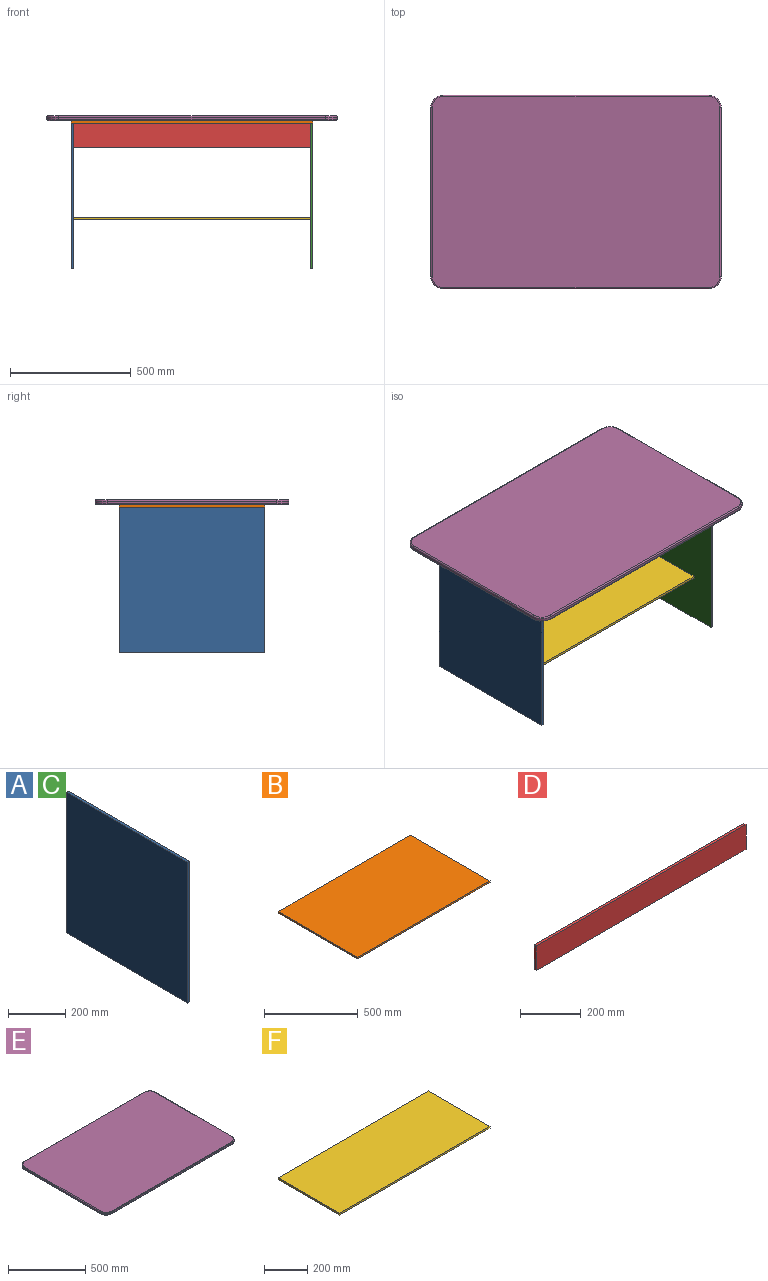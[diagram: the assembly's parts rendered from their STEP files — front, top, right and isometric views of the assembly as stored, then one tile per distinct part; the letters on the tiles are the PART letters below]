
ASSEMBLY  parts=6 mates=5
PART A: 6 faces, bbox 10x600x600 mm
  f0: plane 600x10mm, normal (0,1,0), area 6000mm2, adj f1,f3,f4,f5
  f1: plane 600x10mm, normal (0,0,1), area 6000mm2, adj f0,f2,f4,f5
  f2: plane 600x10mm, normal (0,-1,0), area 6000mm2, adj f1,f3,f4,f5
  f3: plane 600x10mm, normal (0,0,-1), area 6000mm2, adj f0,f2,f4,f5
  f4: plane 600x600mm, normal (1,0,0), area 360000mm2, adj f0,f1,f2,f3
  f5: plane 600x600mm, normal (-1,0,0), area 360000mm2, adj f0,f1,f2,f3
PART B: 6 faces, bbox 1000x600x10 mm
  f0: plane 600x10mm, normal (1,0,0), area 6000mm2, adj f1,f3,f4,f5
  f1: plane 1000x10mm, normal (0,1,0), area 10000mm2, adj f0,f2,f4,f5
  f2: plane 600x10mm, normal (-1,0,0), area 6000mm2, adj f1,f3,f4,f5
  f3: plane 1000x10mm, normal (0,-1,0), area 10000mm2, adj f0,f2,f4,f5
  f4: plane 1000x600mm, normal (0,0,1), area 600000mm2, adj f0,f1,f2,f3
  f5: plane 1000x600mm, normal (0,0,-1), area 600000mm2, adj f0,f1,f2,f3
PART C: same geometry as A
PART D: 6 faces, bbox 980x10x100 mm
  f0: plane 100x10mm, normal (1,0,0), area 1000mm2, adj f1,f3,f4,f5
  f1: plane 980x10mm, normal (0,0,1), area 9800mm2, adj f0,f2,f4,f5
  f2: plane 100x10mm, normal (-1,0,0), area 1000mm2, adj f1,f3,f4,f5
  f3: plane 980x10mm, normal (0,0,-1), area 9800mm2, adj f0,f2,f4,f5
  f4: plane 980x100mm, normal (0,-1,0), area 98000mm2, adj f0,f1,f2,f3
  f5: plane 980x100mm, normal (0,1,0), area 98000mm2, adj f0,f1,f2,f3
PART E: 26 faces, bbox 1208.2x808.2x20 mm
  f0: plane 1100x10mm, normal (0,-1,0), area 11000mm2, adj f6,f9,f15,f24
  f1: plane 700x10mm, normal (1,0,0), area 7000mm2, adj f6,f7,f16,f23
  f2: plane 1100x10mm, normal (0,1,0), area 11000mm2, adj f7,f8,f12,f19
  f3: plane 700x10mm, normal (-1,0,0), area 7000mm2, adj f8,f9,f11,f20
  f4: plane 1190x790mm, normal (0,0,1), area 938361.7mm2, adj f10,f11,f12,f13,f14,f15,f16,f17
  f5: plane 1190x790mm, normal (0,0,-1), area 938361.7mm2, adj f18,f19,f20,f21,f22,f23,f24,f25
  f6: cylinder r=50mm len=50mm, axis (0,0,-1), area 785.4mm2, adj f0,f1,f17,f25
  f7: cylinder r=50mm len=50mm, axis (0,0,1), area 785.4mm2, adj f1,f2,f14,f21
  f8: cylinder r=50mm len=50mm, axis (0,0,-1), area 785.4mm2, adj f2,f3,f10,f18
  f9: cylinder r=50mm len=50mm, axis (0,0,1), area 785.4mm2, adj f0,f3,f13,f22
  f10: torus R=45mm, axis (0,0,1), area 594.4mm2, adj f4,f8,f11,f12
  f11: cylinder r=5mm len=700mm, axis (0,1,0), area 5497.8mm2, adj f3,f4,f10,f13
  f12: cylinder r=5mm len=1100mm, axis (1,0,0), area 8639.4mm2, adj f2,f4,f10,f14
  f13: torus R=45mm, axis (0,0,1), area 594.4mm2, adj f4,f9,f11,f15
  f14: torus R=45mm, axis (0,0,1), area 594.4mm2, adj f4,f7,f12,f16
  f15: cylinder r=5mm len=1100mm, axis (-1,0,0), area 8639.4mm2, adj f0,f4,f13,f17
  f16: cylinder r=5mm len=700mm, axis (0,-1,0), area 5497.8mm2, adj f1,f4,f14,f17
  f17: torus R=45mm, axis (0,0,1), area 594.4mm2, adj f4,f6,f15,f16
  f18: torus R=45mm, axis (0,0,1), area 594.4mm2, adj f5,f8,f19,f20
  f19: cylinder r=5mm len=1100mm, axis (-1,0,0), area 8639.4mm2, adj f2,f5,f18,f21
  f20: cylinder r=5mm len=700mm, axis (0,-1,0), area 5497.8mm2, adj f3,f5,f18,f22
  f21: torus R=45mm, axis (0,0,1), area 594.4mm2, adj f5,f7,f19,f23
  f22: torus R=45mm, axis (0,0,1), area 594.4mm2, adj f5,f9,f20,f24
  f23: cylinder r=5mm len=700mm, axis (0,1,0), area 5497.8mm2, adj f1,f5,f21,f25
  f24: cylinder r=5mm len=1100mm, axis (1,0,0), area 8639.4mm2, adj f0,f5,f22,f25
  f25: torus R=45mm, axis (0,0,1), area 594.4mm2, adj f5,f6,f23,f24
PART F: 6 faces, bbox 980x400x10 mm
  f0: plane 980x10mm, normal (0,-1,0), area 9800mm2, adj f1,f3,f4,f5
  f1: plane 400x10mm, normal (1,0,0), area 4000mm2, adj f0,f2,f4,f5
  f2: plane 980x10mm, normal (0,1,0), area 9800mm2, adj f1,f3,f4,f5
  f3: plane 400x10mm, normal (-1,0,0), area 4000mm2, adj f0,f2,f4,f5
  f4: plane 980x400mm, normal (0,0,1), area 392000mm2, adj f0,f1,f2,f3
  f5: plane 980x400mm, normal (0,0,-1), area 392000mm2, adj f0,f1,f2,f3
PLACE A t=(-495,0,-320)mm
PLACE B t=(0,0,-15)mm
PLACE C t=(495,0,-320)mm
PLACE D t=(0,0,-70)mm
PLACE E at identity fixed
PLACE F t=(0,0,-415)mm
MATE fastened A.f1 <-> B.f5  axis (0,0,1) through (-500,-300,-20)mm
MATE fastened B.f4 <-> E.f5  axis (0,0,1) through (0,0,-10)mm
MATE fastened F.f1 <-> C.f5  axis (1,0,0) through (490,-200,-420)mm
MATE fastened C.f1 <-> B.f5  axis (0,0,1) through (500,300,-20)mm
MATE fastened D.f1 <-> B.f5  axis (0,0,1) through (0,0,-20)mm
